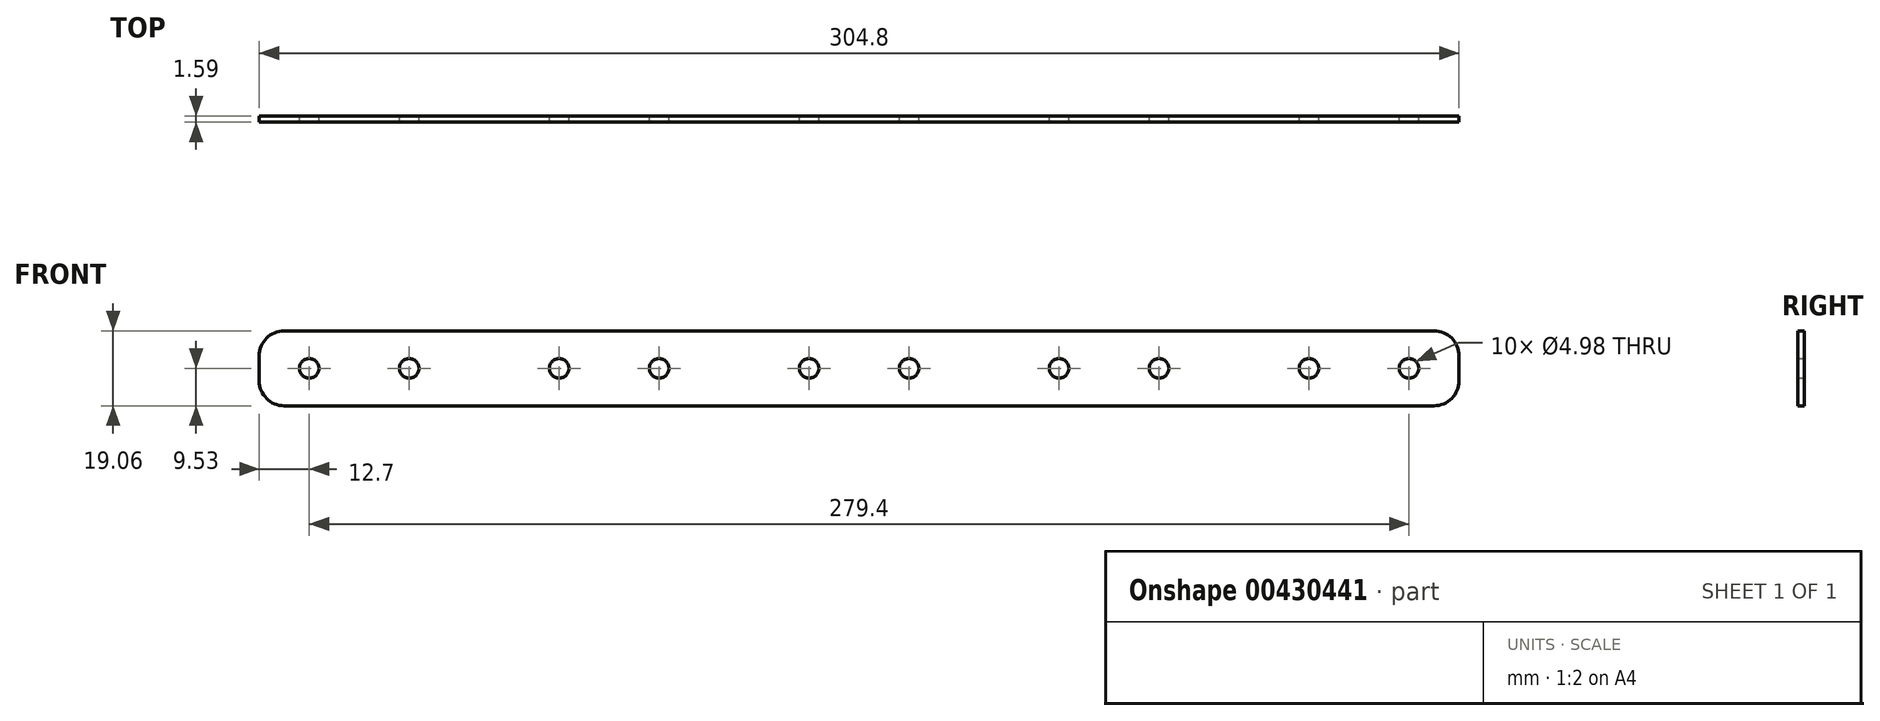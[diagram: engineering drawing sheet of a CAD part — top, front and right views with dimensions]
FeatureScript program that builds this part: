
annotation { "Feature Type Name" : "Feature", "Feature Type Description" : "" }
export const myFeature = defineFeature(function(context is Context, id is Id, definition is map)
    precondition{}
    {
        {
            var Q0;
            Q0=qCreatedBy(makeId("Front.planeOp"),FACE);
            var sketch = newSketch(context, id + "F0", { "sketchPlane" : qUnion([Q0])});
            skLineSegment(sketch, "E0.bottom", {"start": v(-146.05, 9.52) * mm, "end": v(146.05, 9.52) * mm});
            skLineSegment(sketch, "E0.top", {"start": v(-146.05, -9.53) * mm, "end": v(146.05, -9.53) * mm});
            skLineSegment(sketch, "E0.left", {"start": v(-152.4, 3.17) * mm, "end": v(-152.4, -3.18) * mm});
            skLineSegment(sketch, "E0.right", {"start": v(152.4, 3.17) * mm, "end": v(152.4, -3.18) * mm});
            skPoint(sketch, "E0.middle", {"position": v(0, 0) * mm});
            skCircle(sketch, "E1", {"center": v(-12.7, 0) * mm, "radius": 2.49 * mm});
            skCircle(sketch, "E2.MirrorC", {"center": v(12.7, 0) * mm, "radius": 2.49 * mm});
            skPoint(sketch, "E3.visualSharp", {"position": v(-152.4, 9.52) * mm});
            skArc(sketch, "E3.filletArc", {"start": v(-146.05, 9.52) * mm, "mid": v(-150.54, 7.67) * mm, "end": v(-152.4, 3.17) * mm});
            skPoint(sketch, "E4.visualSharp", {"position": v(-152.4, -9.53) * mm});
            skArc(sketch, "E4.filletArc", {"start": v(-152.4, -3.18) * mm, "mid": v(-150.54, -7.67) * mm, "end": v(-146.05, -9.53) * mm});
            skPoint(sketch, "E5.visualSharp", {"position": v(152.4, 9.52) * mm});
            skArc(sketch, "E5.filletArc", {"start": v(152.4, 3.17) * mm, "mid": v(150.54, 7.67) * mm, "end": v(146.05, 9.52) * mm});
            skPoint(sketch, "E6.visualSharp", {"position": v(152.4, -9.53) * mm});
            skArc(sketch, "E6.filletArc", {"start": v(146.05, -9.53) * mm, "mid": v(150.54, -7.67) * mm, "end": v(152.4, -3.18) * mm});
            skCircle(sketch, "E7.1.0.0", {"center": v(50.8, 0) * mm, "radius": 2.49 * mm});
            skCircle(sketch, "E7.1.0.1", {"center": v(76.2, 0) * mm, "radius": 2.49 * mm});
            skLineSegment(sketch, "E7.1.0.2", {"start": v(-82.55, -9.53) * mm, "end": v(209.55, -9.53) * mm});
            skCircle(sketch, "E7.2.0.0", {"center": v(114.3, 0) * mm, "radius": 2.49 * mm});
            skCircle(sketch, "E7.2.0.1", {"center": v(139.7, 0) * mm, "radius": 2.49 * mm});
            skLineSegment(sketch, "E7.2.0.2", {"start": v(-19.05, -9.53) * mm, "end": v(273.05, -9.53) * mm});
            skLineSegment(sketch, "E7.direction1", {"start": v(-12.7, 0) * mm, "end": v(50.8, 0) * mm, "construction": true});
            skCircle(sketch, "E8.MirrorC", {"center": v(-76.2, 0) * mm, "radius": 2.49 * mm});
            skCircle(sketch, "E9.MirrorC", {"center": v(-50.8, 0) * mm, "radius": 2.49 * mm});
            skCircle(sketch, "E10.MirrorC", {"center": v(-114.3, 0) * mm, "radius": 2.49 * mm});
            skCircle(sketch, "E11.MirrorC", {"center": v(-139.7, 0) * mm, "radius": 2.49 * mm});
            skSolve(sketch);
        }
        {
            var Q0;
            Q0 = qSketchRegion(id + "F0", true);
            extrude(context, id + "F1", {"entities" : qUnion([Q0]), "depth" : 1.59 * mm});
        }
    });
